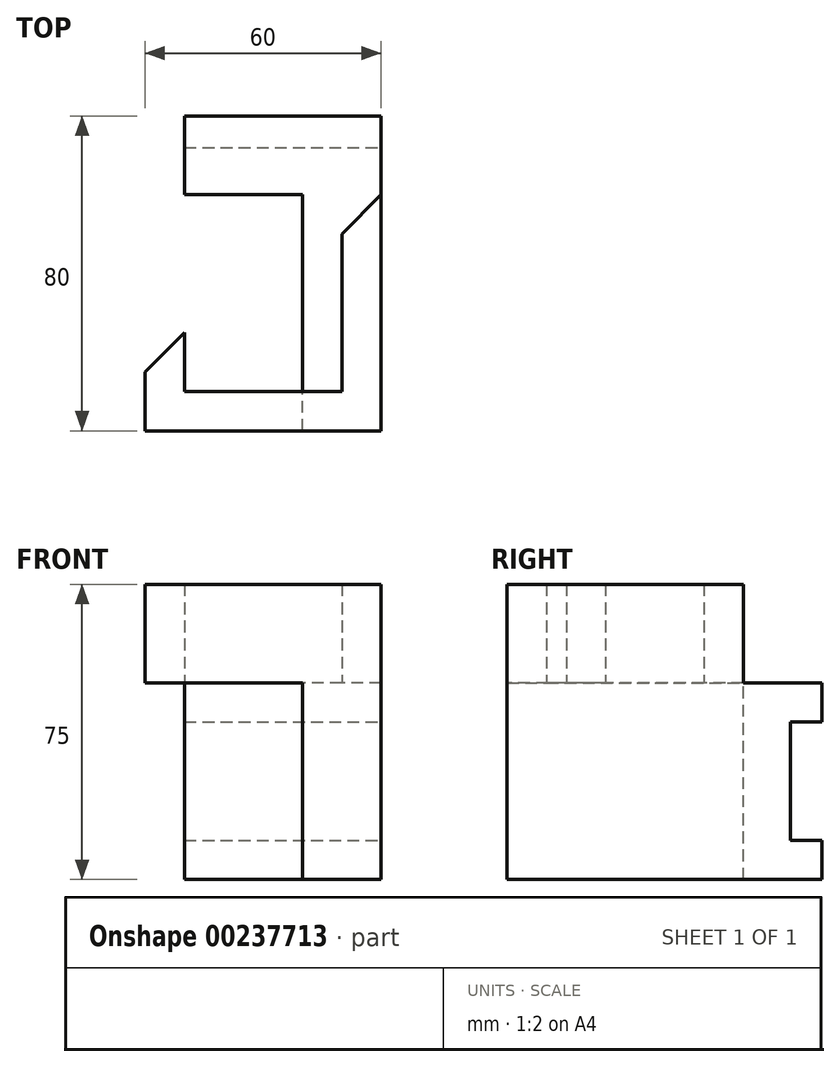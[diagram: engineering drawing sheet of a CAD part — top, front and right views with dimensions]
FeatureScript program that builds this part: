
annotation { "Feature Type Name" : "Feature", "Feature Type Description" : "" }
export const myFeature = defineFeature(function(context is Context, id is Id, definition is map)
    precondition{}
    {
        {
            var Q0;
            Q0=qCreatedBy(makeId("Top.planeOp"),FACE);
            var sketch = newSketch(context, id + "F0", { "sketchPlane" : qUnion([Q0])});
            skLineSegment(sketch, "E0", {"start": v(-60, -60) * mm, "end": v(0, -60) * mm});
            skLineSegment(sketch, "E1", {"start": v(0, -60) * mm, "end": v(0, 0) * mm});
            skLineSegment(sketch, "E2", {"start": v(0, 0) * mm, "end": v(-10, -10) * mm});
            skLineSegment(sketch, "E3", {"start": v(-10, -10) * mm, "end": v(-10, -50) * mm});
            skLineSegment(sketch, "E4", {"start": v(-10, -50) * mm, "end": v(-50, -50) * mm});
            skLineSegment(sketch, "E5", {"start": v(-50, -50) * mm, "end": v(-50, -35) * mm});
            skLineSegment(sketch, "E6", {"start": v(-50, -35) * mm, "end": v(-60, -45) * mm});
            skLineSegment(sketch, "E7", {"start": v(-60, -45) * mm, "end": v(-60, -60) * mm});
            skSolve(sketch);
        }
        {
            var Q0;
            Q0=makeQuery(id+"F0.imprint","IMPRINT",FACE,{"disambiguationData":[TD([[makeQuery(id+"F0.imprint","IMPRINT",EDGE,{"derivedFrom":sQuery(id+"F0.wireOp",EDGE,"E0")}),1.0]])]});
            extrude(context, id + "F1", {"entities" : qUnion([Q0]), "depth" : 25 * mm});
        }
        {
            var Q0;
            Q0=qCreatedBy(makeId("Right.planeOp"),FACE);
            var sketch = newSketch(context, id + "F2", { "sketchPlane" : qUnion([Q0])});
            skLineSegment(sketch, "E8.bottom", {"start": v(-60, -50) * mm, "end": v(0, -50) * mm});
            skLineSegment(sketch, "E8.top", {"start": v(-60, 0) * mm, "end": v(0, 0) * mm});
            skLineSegment(sketch, "E8.left", {"start": v(-60, -50) * mm, "end": v(-60, 0) * mm});
            skLineSegment(sketch, "E8.right", {"start": v(0, -50) * mm, "end": v(0, 0) * mm});
            skLineSegment(sketch, "E9.bottom", {"start": v(0, -50) * mm, "end": v(20, -50) * mm});
            skLineSegment(sketch, "E9.top", {"start": v(0, 0) * mm, "end": v(20, 0) * mm});
            skLineSegment(sketch, "E9.right", {"start": v(20, -50) * mm, "end": v(20, 0) * mm});
            skLineSegment(sketch, "E10.bottom", {"start": v(20, -40) * mm, "end": v(12, -40) * mm});
            skLineSegment(sketch, "E10.top", {"start": v(20, -10) * mm, "end": v(12, -10) * mm});
            skLineSegment(sketch, "E10.left", {"start": v(20, -40) * mm, "end": v(20, -10) * mm});
            skLineSegment(sketch, "E10.right", {"start": v(12, -40) * mm, "end": v(12, -10) * mm});
            skSolve(sketch);
        }
        {
            var Q0;
            Q0=makeQuery(id+"F2.imprint","IMPRINT",FACE,{"disambiguationData":[TD([[makeQuery(id+"F2.imprint","IMPRINT",EDGE,{"derivedFrom":sQuery(id+"F2.wireOp",EDGE,"E8.bottom")}),1.0]])]});
            extrude(context, id + "F3", {"entities" : qUnion([Q0]), "oppositeDirection" : true, "depth" : 20 * mm});
        }
        {
            var Q0;
            {var subQ1=sQuery(id+"F2.wireOp",EDGE,"E9.bottom");Q0=makeQuery(id+"F2.imprint","IMPRINT",FACE,{"disambiguationData":[TD([[makeQuery(id+"F2.imprint","IMPRINT",EDGE,{"derivedFrom":subQ1}),1.0]])]});}
            extrude(context, id + "F4", {"entities" : qUnion([Q0]), "operationType" : NewBodyOperationType.ADD, "oppositeDirection" : true, "depth" : 50 * mm});
        }
    });
